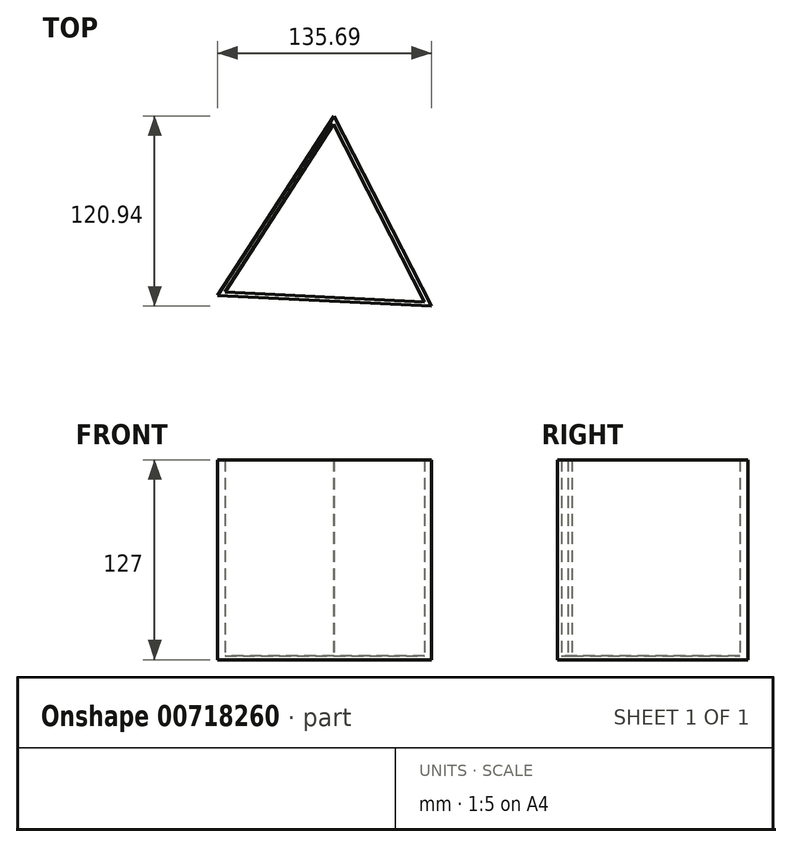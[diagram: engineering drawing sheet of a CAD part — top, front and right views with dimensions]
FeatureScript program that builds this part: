
annotation { "Feature Type Name" : "Feature", "Feature Type Description" : "" }
export const myFeature = defineFeature(function(context is Context, id is Id, definition is map)
    precondition{}
    {
        {
            var Q0;
            Q0=qCreatedBy(makeId("Top.planeOp"),FACE);
            var sketch = newSketch(context, id + "F0", { "sketchPlane" : qUnion([Q0])});
            skCircle(sketch, "E0.cCircle", {"center": v(0, 0) * mm, "radius": 39.22 * mm, "construction": true});
            skLineSegment(sketch, "E0.0", {"start": v(3.96, 78.34) * mm, "end": v(65.87, -42.6) * mm});
            skLineSegment(sketch, "E0.1", {"start": v(65.87, -42.6) * mm, "end": v(-69.82, -35.75) * mm});
            skLineSegment(sketch, "E0.2", {"start": v(-69.82, -35.75) * mm, "end": v(3.96, 78.34) * mm});
            skPoint(sketch, "E0.0.midPoint", {"position": v(34.91, 17.87) * mm});
            skSolve(sketch);
        }
        {
            var Q0;
            Q0 = qSketchRegion(id + "F0", true);
            extrude(context, id + "F1", {"entities" : qUnion([Q0]), "depth" : 127 * mm, "offsetDistance" : 25.4 * mm});
        }
        {
            var Q0;
            Q0=makeQuery(id+"F1.opExtrude","CAP_FACE",FACE,{"disambiguationData":[OSD([sQuery(id+"F0.wireOp",EDGE,"E0.0"),sQuery(id+"F0.wireOp",EDGE,"E0.1"),sQuery(id+"F0.wireOp",EDGE,"E0.2")])],"isStart":false});
            shell(context, id + "F2", {"entities" : qUnion([Q0]), "thickness" : 2.54 * mm});
        }
    });
